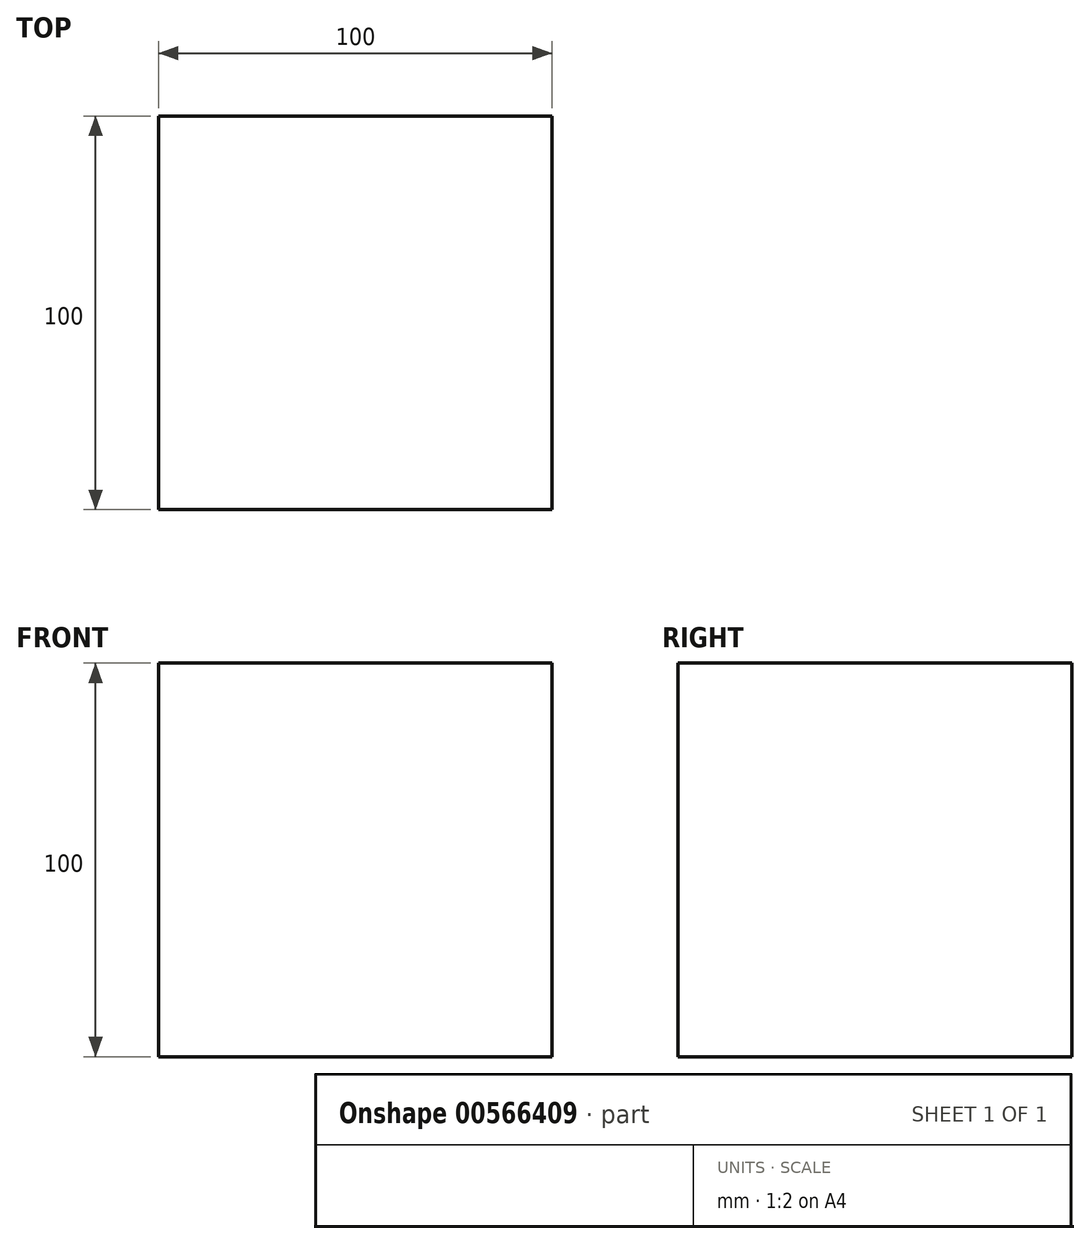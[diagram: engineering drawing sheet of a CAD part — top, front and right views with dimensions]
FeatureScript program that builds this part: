
annotation { "Feature Type Name" : "Feature", "Feature Type Description" : "" }
export const myFeature = defineFeature(function(context is Context, id is Id, definition is map)
    precondition{}
    {
        {
            var Q0;
            Q0=qCreatedBy(makeId("Front.planeOp"),FACE);
            var sketch = newSketch(context, id + "F0", { "sketchPlane" : qUnion([Q0])});
            skLineSegment(sketch, "E0.bottom", {"start": v(10, 120) * mm, "end": v(110, 120) * mm});
            skLineSegment(sketch, "E0.top", {"start": v(10, 20) * mm, "end": v(110, 20) * mm});
            skLineSegment(sketch, "E0.left", {"start": v(10, 120) * mm, "end": v(10, 20) * mm});
            skLineSegment(sketch, "E0.right", {"start": v(110, 120) * mm, "end": v(110, 20) * mm});
            skSolve(sketch);
        }
        {
            var Q0;
            Q0=makeQuery(id+"F0.imprint","IMPRINT",FACE,{"disambiguationData":[TD([[makeQuery(id+"F0.imprint","IMPRINT",EDGE,{"derivedFrom":sQuery(id+"F0.wireOp",EDGE,"E0.bottom")}),-1.0]])]});
            var Q1;
            Q1=sQuery(id+"F0.wireOp",EDGE,"E0.right");
            var Q2;
            Q2=sQuery(id+"F0.wireOp",EDGE,"E0.bottom");
            var Q3;
            Q3=sQuery(id+"F0.wireOp",EDGE,"E0.top");
            var Q4;
            Q4=sQuery(id+"F0.wireOp",EDGE,"E0.left");
            extrude(context, id + "F1", {"entities" : qUnion([Q0]), "surfaceEntities" : qUnion([Q1, Q2, Q3, Q4]), "depth" : 100 * mm, "offsetDistance" : 25 * mm});
        }
    });
